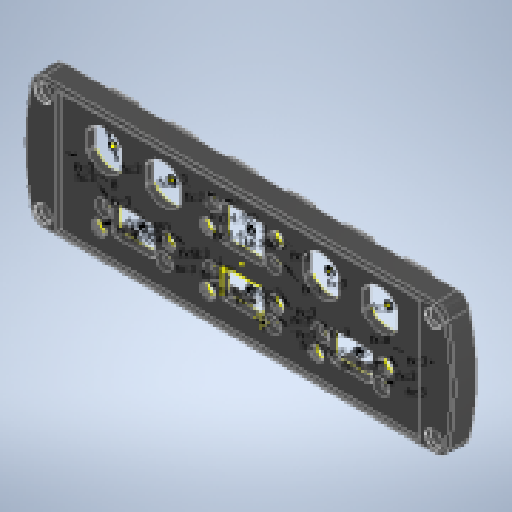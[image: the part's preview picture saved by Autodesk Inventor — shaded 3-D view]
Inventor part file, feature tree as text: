
AUTODESK INVENTOR PART (.ipt)
format: ipt  version: 2024 (Build 280153000, 153)  size: 1,394,688 bytes
history: native  units: mm
features: extrude x8, sketch x7, fillet x4, chamfer x4, plane x2, mirror x1, hole x1, other x1
ambient origin geometry x8: Origin, YZ Plane, XZ Plane, XY Plane, X Axis, Y Axis, Z Axis, Center Point
bodies: Solid1 (feature_tree)
feature tree (28):
  extrude  "Extrusion1"  TaperAngle=0.0deg  [1 undecoded]
  fillet  "Fillet1"  Radius=6.9mm
  plane  "Work Plane1"
  extrude  "Extrusion4"  [1 undecoded]
  fillet  "Fillet6"  Radius=15.4mm
  chamfer  "Chamfer2"  [1 undecoded]
  mirror  "Mirror1"
  plane  "Work Plane2"
  extrude  "Extrusion7"  Depth=0.2mm TaperAngle=45.0deg
  extrude  "Extrusion11"  Depth=1.5mm
  extrude  "Extrusion12"  Depth=1.5mm
  fillet  "Fillet4"  Radius=10.075mm
  chamfer  "Chamfer4"  Distance=42.584mm
  extrude  "Extrusion13"  Depth=1.5mm
  extrude  "Extrusion14"  Depth=10.0mm TaperAngle=0.0deg
  fillet  "Fillet5"  Radius=0.5mm
  extrude  "Extrusion15"  Depth=1.5mm
  chamfer  "Chamfer5"  Distance=10.075mm
  hole  "Hole1"  [1 undecoded]
  chamfer  "Chamfer3"  Distance=6.9mm
  sketch  "Sketch20"  dims[d3=9.0mm d15=0.0mm d16=0.0mm d21=6.9mm]
  sketch  "Sketch21"  dims[d23=1.35mm d26=-1.5mm d40=15.4mm]
  sketch  "Sketch24"  dims[d43=15.4mm]
  sketch  "Sketch25"  dims[d44=0.0mm]
  sketch  "Sketch27"  dims[d45=31.0mm d46=0.0mm d47=0.0mm d48=0.2mm d49=2.0mm d50=45.0deg d65=4.85mm d66=4.85mm d67=27.0mm d68=9.0mm d69=3.3mm d70=3.3mm d71=24.0mm d72=16.55mm d73=11.55mm d74=6.35mm d75=1.85mm d76=5.225mm d77=6.9mm d78=10.075mm d79=10.075mm d80=42.584mm d82=7.0mm d83=10.0mm d84=0.0mm d85=0.5mm d86=2.0mm d87=45.0deg d101=10.075mm d102=4.85mm d103=4.85mm d104=27.0mm d105=9.0mm d106=3.3mm d107=3.3mm d108=24.0mm d109=16.55mm d110=11.55mm d111=6.35mm d112=1.85mm d113=5.225mm d114=10.075mm d115=12.0mm d116=6.9mm d117=42.584mm d118=7.0mm d119=7.0mm d122=12.0mm d127=3.25mm d128=6.0mm d129=6.25mm d130=2.0mm d131=90.0deg d132=8.0mm d133=20.594885mm d136=10.0mm d137=0.0mm d138=0.2mm d139=0.0mm d140=3.0mm d141=0.2mm d142=2.0mm d143=45.0deg d144=0.2mm d145=2.0mm d146=45.0deg d147=10.0mm d148=0.0mm d149=8.0mm d150=12.5mm d151=8.0mm d152=12.5mm d153=12.5mm d154=8.0mm d155=8.0mm d156=12.5mm d157=4.5mm d160=4.5mm d161=1.0mm d164=1.0mm d167=28.699852mm d169=20.0mm d171=42.584mm d172=10.0mm d174=10.0mm d176=7.0mm d177=7.0mm d178=7.0mm d179=1.0mm d180=4.5mm d181=7.001437mm d182=16.55mm d183=14.55mm d184=3.3mm d185=4.85mm d186=4.85mm d187=3.3mm d188=5.225mm d189=9.0mm d190=4.5mm d191=27.0mm d192=24.0mm d193=3.725mm d194=9.0mm d195=4.5mm d197=9.125mm d198=10.0mm d199=0.0mm d200=1.35mm d201=7.0mm d202=7.0mm d203=1.9mm d204=0.0mm d205=0.0mm d206=8.871486mm d207=3.839257mm d208=16.55mm d209=13.6mm d210=6.8mm d211=13.6mm d212=6.8mm d213=1.5mm d214=16.95mm d215=11.95mm d216=5.975mm d217=8.475mm d218=8.475mm d219=5.975mm d220=8.475mm d221=5.975mm d222=16.95mm d223=14.95mm d224=8.475mm d225=7.475mm d226=3.0mm d227=3.0mm d228=3.0mm d229=3.0mm d230=3.0mm d231=3.0mm d232=3.0mm d233=3.0mm d234=3.0mm d235=3.0mm d236=3.0mm d237=3.0mm d239=3.0mm d240=3.0mm d241=3.0mm d242=3.0mm d243=3.0mm d244=3.0mm d245=3.0mm d246=3.0mm d247=3.0mm d248=3.0mm d249=3.0mm d250=3.0mm d251=8.0mm d252=8.0mm d253=3.0mm d254=3.0mm]
  sketch  "Sketch22"  dims[d41=11.5mm]
  sketch  "Sketch23"  dims[d42=54.0mm]
  other  "1009799_3D"
note: 4 required parameter values undecoded (feature->parameter linkage not recoverable at this tier; creation-order binding heuristic only, values carry confidence <= 0.55)
